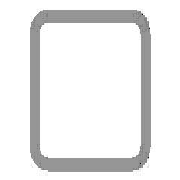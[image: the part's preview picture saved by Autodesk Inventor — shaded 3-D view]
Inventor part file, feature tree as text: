
AUTODESK INVENTOR PART (.ipt)
format: ipt  version: 2024 (Build 280153000, 153)  size: 128,512 bytes
history: native  units: mm (DEFAULTED — no unit token found)
features: other x4, extrude x1, sketch x1, plane x1
ambient origin geometry x8: Origin, YZ Plane, XZ Plane, XY Plane, X Axis, Y Axis, Z Axis, Center Point
bodies: Solid1 (feature_tree)
feature tree (7):
  parser-record x1  (decoder bookkeeping rows leaked as tree rows — omitted from the tree; the rows remain in map.json)
  other  "Driven Length"
  other  "Plano inicial"
  other  "Plano final"
  extrude  "Cuerpo"  TaperAngle=0.0deg  [1 undecoded]
  sketch  "Sketch3"  dims[d3=1700.0mm d4=0.0mm d10=50.8mm d11=50.8mm d12=3.175mm d13=-0.0mm d14=1700.0mm d15=25.4mm d16=25.4mm d17=6.35mm d18=90.0deg d19=1700.0mm]
  plane  "Work Plane3"
note: 1 required parameter value undecoded (feature->parameter linkage not recoverable at this tier; creation-order binding heuristic only, values carry confidence <= 0.55)
